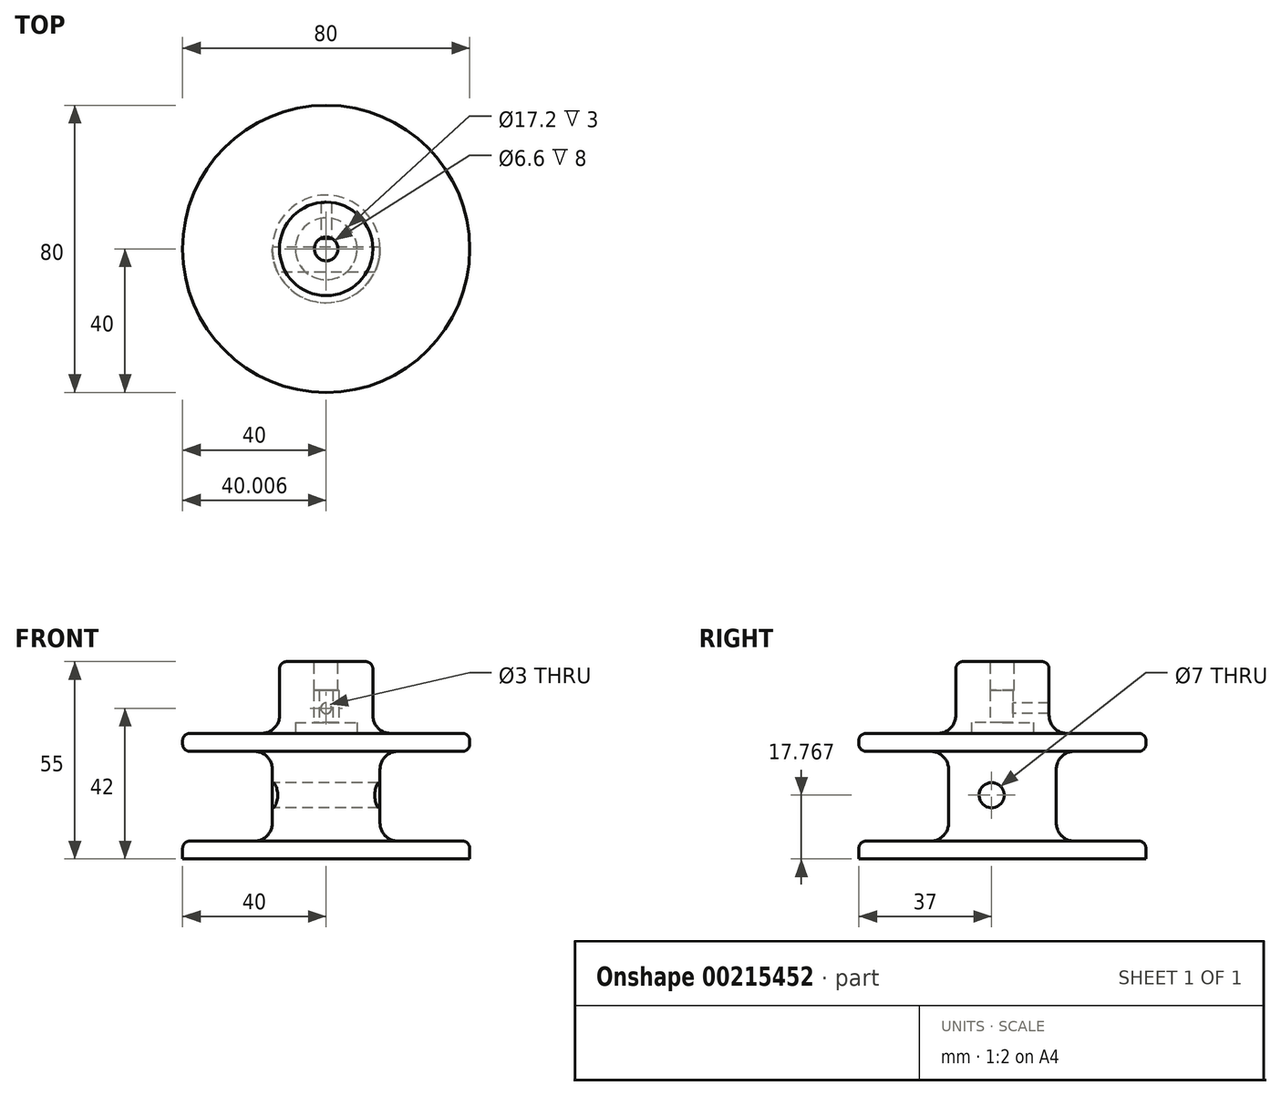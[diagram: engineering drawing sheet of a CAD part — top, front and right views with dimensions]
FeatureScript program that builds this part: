
annotation { "Feature Type Name" : "Feature", "Feature Type Description" : "" }
export const myFeature = defineFeature(function(context is Context, id is Id, definition is map)
    precondition{}
    {
        {
            var Q0;
            Q0=qCreatedBy(makeId("Top.planeOp"),FACE);
            var sketch = newSketch(context, id + "F0", { "sketchPlane" : qUnion([Q0])});
            skCircle(sketch, "E0", {"center": v(0, 0) * mm, "radius": 13 * mm});
            skSolve(sketch);
        }
        {
            var Q0;
            Q0=qCreatedBy(makeId("Top.planeOp"),FACE);
            cPlane(context, id + "F1", {"entities" : qUnion([Q0]), "cplaneType" : CPlaneType.OFFSET, "offset" : 20 * mm, "width" : 150 * mm, "height" : 150 * mm});
        }
        {
            var Q0;
            Q0=qCreatedBy(makeId("Top.planeOp"),FACE);
            cPlane(context, id + "F2", {"entities" : qUnion([Q0]), "cplaneType" : CPlaneType.OFFSET, "offset" : 20 * mm, "oppositeDirection" : true, "width" : 150 * mm, "height" : 150 * mm});
        }
        {
            var Q0;
            Q0=qCreatedBy(id+"F1.planeOp",FACE);
            var sketch = newSketch(context, id + "F3", { "sketchPlane" : qUnion([Q0])});
            skCircle(sketch, "E1", {"center": v(0, 0) * mm, "radius": 3.3 * mm});
            skSolve(sketch);
        }
        {
            var Q0;
            Q0=qCreatedBy(id+"F2.planeOp",FACE);
            var sketch = newSketch(context, id + "F4", { "sketchPlane" : qUnion([Q0])});
            skCircle(sketch, "E2", {"center": v(0, 0) * mm, "radius": 8.6 * mm});
            skSolve(sketch);
        }
        {
            var Q0;
            Q0=qSketchRegion(id+"F0",true);
            extrude(context, id + "F5", {"entities" : qUnion([Q0]), "offsetDistance" : 25 * mm, "depth" : 40 * mm, "symmetric" : true});
        }
        {
            var Q0;
            Q0=qSketchRegion(id+"F4",true);
            extrude(context, id + "F6", {"entities" : qUnion([Q0]), "operationType" : NewBodyOperationType.REMOVE, "depth" : 23 * mm});
        }
        {
            var Q0;
            Q0=qCreatedBy(makeId("Top.planeOp"),FACE);
            var sketch = newSketch(context, id + "F7", { "sketchPlane" : qUnion([Q0])});
            skLineSegment(sketch, "E3", {"start": v(0, 2.95) * mm, "end": v(-1.89, 2.95) * mm});
            skLineSegment(sketch, "E4", {"start": v(-1.89, 2.95) * mm, "end": v(1.89, 2.95) * mm});
            skArc(sketch, "E5", {"start": v(-1.89, 2.95) * mm, "mid": v(0, -3.5) * mm, "end": v(1.89, 2.95) * mm});
            skSolve(sketch);
        }
        {
            var Q0;
            Q0=qSketchRegion(id+"F3",true);
            extrude(context, id + "F8", {"entities" : qUnion([Q0]), "operationType" : NewBodyOperationType.REMOVE, "oppositeDirection" : true, "depth" : 8 * mm});
        }
        {
            var Q0;
            Q0=qSketchRegion(id+"F7",true);
            extrude(context, id + "F9", {"entities" : qUnion([Q0]), "operationType" : NewBodyOperationType.REMOVE, "depth" : 12 * mm});
        }
        {
            var Q0;
            Q0=qCreatedBy(makeId("Right.planeOp"),FACE);
            var sketch = newSketch(context, id + "F10", { "sketchPlane" : qUnion([Q0])});
            skCircle(sketch, "E6", {"center": v(-2.5, -12.5) * mm, "radius": 2.05 * mm});
            skSolve(sketch);
        }
        {
            var Q0;
            Q0=qSketchRegion(id+"F10",true);
            extrude(context, id + "F11", {"entities" : qUnion([Q0]), "operationType" : NewBodyOperationType.REMOVE, "oppositeDirection" : true, "offsetDistance" : 25 * mm, "depth" : 100 * mm, "symmetric" : true});
        }
        {
            var Q0;
            Q0=qCreatedBy(makeId("Front.planeOp"),FACE);
            var sketch = newSketch(context, id + "F12", { "sketchPlane" : qUnion([Q0])});
            skCircle(sketch, "E7", {"center": v(0, 7) * mm, "radius": 1.5 * mm});
            skSolve(sketch);
        }
        {
            var Q0;
            Q0=qSketchRegion(id+"F12",true);
            extrude(context, id + "F13", {"entities" : qUnion([Q0]), "operationType" : NewBodyOperationType.REMOVE, "oppositeDirection" : true, "depth" : 25 * mm});
        }
        {
            var Q0;
            Q0=qCreatedBy(makeId("Right.planeOp"),FACE);
            cPlane(context, id + "F14", {"entities" : qUnion([Q0]), "cplaneType" : CPlaneType.OFFSET, "offset" : 11 * mm, "width" : 150 * mm, "height" : 150 * mm});
        }
        {
            var Q0;
            Q0=qCreatedBy(id+"F14.planeOp",FACE);
            var sketch = newSketch(context, id + "F15", { "sketchPlane" : qUnion([Q0])});
            skCircle(sketch, "E8", {"center": v(-2.5, -12.5) * mm, "radius": 3.5 * mm});
            skSolve(sketch);
        }
        {
            var Q0;
            Q0=qSketchRegion(id+"F15",true);
            extrude(context, id + "F16", {"entities" : qUnion([Q0]), "operationType" : NewBodyOperationType.REMOVE, "depth" : 5 * mm});
        }
        {
            var Q0;
            Q0=qCreatedBy(makeId("Right.planeOp"),FACE);
            cPlane(context, id + "F17", {"entities" : qUnion([Q0]), "cplaneType" : CPlaneType.OFFSET, "offset" : 12 * mm, "oppositeDirection" : true, "width" : 150 * mm, "height" : 150 * mm});
        }
        {
            var Q0;
            Q0=qCreatedBy(id+"F17.planeOp",FACE);
            var sketch = newSketch(context, id + "F18", { "sketchPlane" : qUnion([Q0])});
            skCircle(sketch, "E9.cCircle", {"center": v(-2.5, -12.5) * mm, "radius": 3.8 * mm, "construction": true});
            skLineSegment(sketch, "E9.0", {"start": v(-5.6, -14.68) * mm, "end": v(-5.95, -10.9) * mm});
            skLineSegment(sketch, "E9.1", {"start": v(-5.95, -10.9) * mm, "end": v(-2.84, -8.71) * mm});
            skLineSegment(sketch, "E9.2", {"start": v(-2.84, -8.71) * mm, "end": v(0.6, -10.32) * mm});
            skLineSegment(sketch, "E9.3", {"start": v(0.6, -10.32) * mm, "end": v(0.95, -14.1) * mm});
            skLineSegment(sketch, "E9.4", {"start": v(0.95, -14.1) * mm, "end": v(-2.16, -16.29) * mm});
            skLineSegment(sketch, "E9.5", {"start": v(-2.16, -16.29) * mm, "end": v(-5.6, -14.68) * mm});
            skSolve(sketch);
        }
        {
            var Q0;
            Q0=qSketchRegion(id+"F18",true);
            extrude(context, id + "F19", {"entities" : qUnion([Q0]), "operationType" : NewBodyOperationType.REMOVE, "oppositeDirection" : true, "offsetDistance" : 25 * mm, "depth" : 3 * mm});
        }
        {
            var Q0;
            Q0=qCreatedBy(makeId("Right.planeOp"),FACE);
            var sketch = newSketch(context, id + "F20", { "sketchPlane" : qUnion([Q0])});
            skLineSegment(sketch, "E10", {"start": v(0, -35) * mm, "end": v(40, -35) * mm});
            skLineSegment(sketch, "E11", {"start": v(40, -35) * mm, "end": v(40, -30) * mm});
            skLineSegment(sketch, "E12", {"start": v(40, -30) * mm, "end": v(15, -30) * mm});
            skLineSegment(sketch, "E13", {"start": v(15, -30) * mm, "end": v(15, -5) * mm});
            skLineSegment(sketch, "E14", {"start": v(15, -5) * mm, "end": v(40, -5) * mm});
            skLineSegment(sketch, "E15", {"start": v(40, -5) * mm, "end": v(40, 0) * mm});
            skLineSegment(sketch, "E16", {"start": v(40, 0) * mm, "end": v(0, 0) * mm});
            skLineSegment(sketch, "E17", {"start": v(0, 0) * mm, "end": v(0, -35) * mm});
            skSolve(sketch);
        }
        {
            var Q0;
            Q0 = qSketchRegion(id + "F20", true);
            var Q1;
            Q1=sQuery(id+"F20.wireOp",EDGE,"E17");
            revolve(context, id + "F21", {"operationType" : NewBodyOperationType.ADD, "surfaceOperationType" : NewSurfaceOperationType.NEW, "entities" : qUnion([Q0]), "axis" : qUnion([Q1]), "revolveType" : RevolveType.FULL});
        }
        {
            var Q0;
            Q0=qCreatedBy(makeId("Right.planeOp"),FACE);
            var sketch = newSketch(context, id + "F22", { "sketchPlane" : qUnion([Q0])});
            skCircle(sketch, "E18", {"center": v(-3, -17.23) * mm, "radius": 3.5 * mm});
            skSolve(sketch);
        }
        {
            var Q0;
            Q0 = qSketchRegion(id + "F22", true);
            extrude(context, id + "F23", {"entities" : qUnion([Q0]), "operationType" : NewBodyOperationType.REMOVE, "depth" : 125 * mm, "offsetDistance" : 25 * mm, "symmetric" : true});
        }
        {
            var Q0;
            Q0=makeQuery(id+"F21.opRevolve","SWEPT_EDGE",EDGE,{"disambiguationData":[OSD([sQuery(id+"F20.wireOp",EDGE,"E13"),sQuery(id+"F20.wireOp",EDGE,"E14")])]});
            var Q1;
            Q1=makeQuery(id+"F21.opRevolve","SWEPT_EDGE",EDGE,{"disambiguationData":[OSD([sQuery(id+"F20.wireOp",EDGE,"E12"),sQuery(id+"F20.wireOp",EDGE,"E13")])]});
            var Q2;
            Q2=makeQuery(id+"F21.boolean.opBoolean","INTERSECT",EDGE,{"derivedFrom":[makeQuery(id+"F5.opExtrude","SWEPT_FACE",FACE,{"disambiguationData":[OSD([sQuery(id+"F0.wireOp",EDGE,"E0")])]}),makeQuery(id+"F21.opRevolve","SWEPT_FACE",FACE,{"disambiguationData":[OSD([sQuery(id+"F20.wireOp",EDGE,"E16")])]})]});
            fillet(context, id + "F24", {"entities" : qUnion([Q0, Q1, Q2]), "tangentPropagation" : true, "radius" : 5 * mm, "defaultsChanged" : false, "vertexSettings" : [], "allowEdgeOverflow" : false});
        }
        {
            var Q0;
            Q0=makeQuery(id+"F21.opRevolve","SWEPT_EDGE",EDGE,{"disambiguationData":[OSD([sQuery(id+"F20.wireOp",EDGE,"E15"),sQuery(id+"F20.wireOp",EDGE,"E16")])]});
            var Q1;
            Q1=makeQuery(id+"F21.opRevolve","SWEPT_EDGE",EDGE,{"disambiguationData":[OSD([sQuery(id+"F20.wireOp",EDGE,"E14"),sQuery(id+"F20.wireOp",EDGE,"E15")])]});
            var Q2;
            Q2=makeQuery(id+"F21.opRevolve","SWEPT_EDGE",EDGE,{"disambiguationData":[OSD([sQuery(id+"F20.wireOp",EDGE,"E11"),sQuery(id+"F20.wireOp",EDGE,"E12")])]});
            var Q3;
            Q3=makeQuery(id+"F5.opExtrude","CAP_EDGE",EDGE,{"disambiguationData":[OSD([sQuery(id+"F0.wireOp",EDGE,"E0")])],"isStart":false});
            fillet(context, id + "F25", {"entities" : qUnion([Q0, Q1, Q2, Q3]), "tangentPropagation" : true, "radius" : 2 * mm, "defaultsChanged" : false, "vertexSettings" : [], "allowEdgeOverflow" : false});
        }
    });
